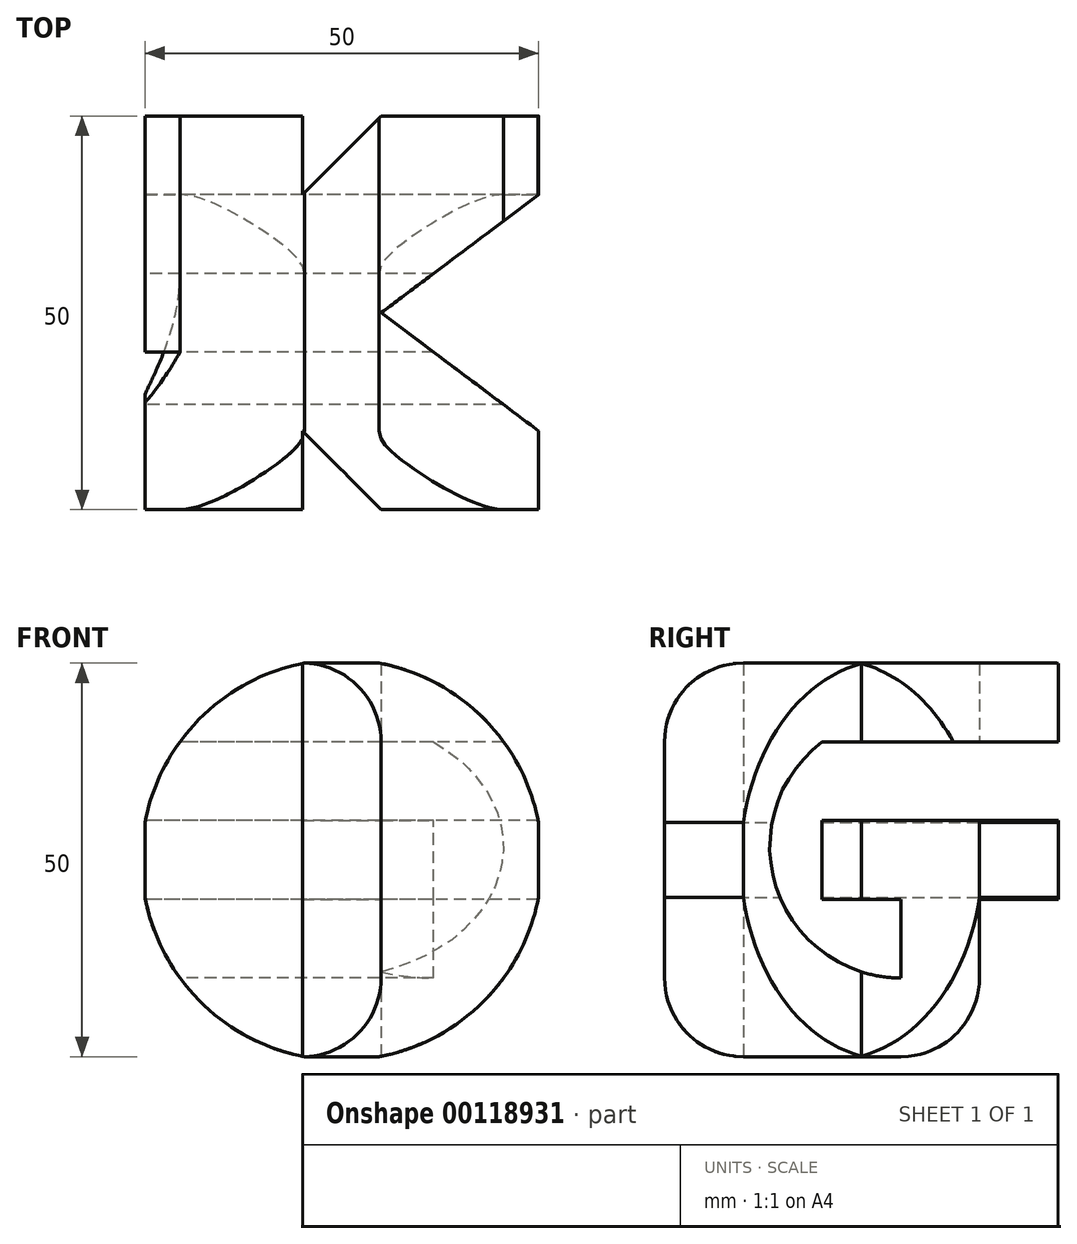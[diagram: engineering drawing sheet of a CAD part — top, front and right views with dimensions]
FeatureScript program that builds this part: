
annotation { "Feature Type Name" : "Feature", "Feature Type Description" : "" }
export const myFeature = defineFeature(function(context is Context, id is Id, definition is map)
    precondition{}
    {
        {
            var Q0;
            Q0=qCreatedBy(makeId("Top.planeOp"),FACE);
            var sketch = newSketch(context, id + "F0", { "sketchPlane" : qUnion([Q0])});
            skLineSegment(sketch, "E0", {"start": v(-25, 25) * mm, "end": v(-25, -25) * mm});
            skLineSegment(sketch, "E1", {"start": v(-25, -25) * mm, "end": v(-5, -25) * mm});
            skLineSegment(sketch, "E2", {"start": v(-5, -15) * mm, "end": v(-5, -25) * mm});
            skLineSegment(sketch, "E3", {"start": v(-5, -15) * mm, "end": v(5, -25) * mm});
            skLineSegment(sketch, "E4", {"start": v(5, -25) * mm, "end": v(25, -25) * mm});
            skLineSegment(sketch, "E5", {"start": v(25, 15) * mm, "end": v(25, 25) * mm});
            skLineSegment(sketch, "E6", {"start": v(-5, 25) * mm, "end": v(-25, 25) * mm});
            skLineSegment(sketch, "E7", {"start": v(-5, 15) * mm, "end": v(5, 25) * mm});
            skLineSegment(sketch, "E8", {"start": v(5, 0) * mm, "end": v(25, -15) * mm});
            skLineSegment(sketch, "E9", {"start": v(25, 15) * mm, "end": v(5, 0) * mm});
            skLineSegment(sketch, "E10", {"start": v(25, -25) * mm, "end": v(25, -15) * mm});
            skLineSegment(sketch, "E11", {"start": v(-5, 15) * mm, "end": v(-5, 25) * mm});
            skLineSegment(sketch, "E12", {"start": v(5, 25) * mm, "end": v(25, 25) * mm});
            skSolve(sketch);
        }
        {
            var Q0;
            Q0=qCreatedBy(makeId("Right.planeOp"),FACE);
            var sketch = newSketch(context, id + "F1", { "sketchPlane" : qUnion([Q0])});
            skLineSegment(sketch, "E13", {"start": v(25, 15) * mm, "end": v(25, 15) * mm});
            skLineSegment(sketch, "E14", {"start": v(25, 15) * mm, "end": v(5, 15) * mm});
            skLineSegment(sketch, "E15", {"start": v(-5, 5) * mm, "end": v(-5, -5) * mm});
            skLineSegment(sketch, "E16", {"start": v(5, -15) * mm, "end": v(5, -15) * mm});
            skLineSegment(sketch, "E17", {"start": v(15, -5) * mm, "end": v(15, -5) * mm});
            skLineSegment(sketch, "E18", {"start": v(-25, 15) * mm, "end": v(-25, -15) * mm});
            skArc(sketch, "E19.filletArc", {"start": v(-15, 25) * mm, "mid": v(-22.07, 22.07) * mm, "end": v(-25, 15) * mm});
            skPoint(sketch, "E20.visualSharp", {"position": v(15, -15) * mm});
            skPoint(sketch, "E21.visualSharp", {"position": v(-5, 15) * mm});
            skArc(sketch, "E22.filletArc", {"start": v(-25, -15) * mm, "mid": v(-22.07, -22.07) * mm, "end": v(-15, -25) * mm});
            skLineSegment(sketch, "E23", {"start": v(25, 15) * mm, "end": v(25, 25) * mm});
            skLineSegment(sketch, "E24", {"start": v(5, -5) * mm, "end": v(5, -15) * mm});
            skLineSegment(sketch, "E25", {"start": v(15, -15) * mm, "end": v(15, -5) * mm});
            skLineSegment(sketch, "E26", {"start": v(15, -5) * mm, "end": v(25, -5) * mm});
            skLineSegment(sketch, "E27", {"start": v(-5, -5) * mm, "end": v(5, -5) * mm});
            skArc(sketch, "E28", {"start": v(5, -25) * mm, "mid": v(12.07, -22.07) * mm, "end": v(15, -15) * mm});
            skLineSegment(sketch, "E29", {"start": v(-15, -25) * mm, "end": v(5, -25) * mm});
            skArc(sketch, "E30", {"start": v(-10, -5) * mm, "mid": v(-4.01, -12.27) * mm, "end": v(5, -15) * mm});
            skArc(sketch, "E31", {"start": v(-5, 15) * mm, "mid": v(-10.81, -3.6) * mm, "end": v(5, -15) * mm});
            skLineSegment(sketch, "E32", {"start": v(-5, 15) * mm, "end": v(25, 15) * mm});
            skLineSegment(sketch, "E33", {"start": v(25, 5) * mm, "end": v(25, -5) * mm});
            skLineSegment(sketch, "E34", {"start": v(-15, 25) * mm, "end": v(25, 25) * mm});
            skLineSegment(sketch, "E35", {"start": v(-5, 5) * mm, "end": v(25, 5) * mm});
            skSolve(sketch);
        }
        {
            var Q0;
            Q0 = qSketchRegion(id + "F0", true);
            extrude(context, id + "F2", {"entities" : qUnion([Q0]), "endBound" : BoundingType.SYMMETRIC, "depth" : 50 * mm});
        }
        {
            var Q0;
            Q0 = qSketchRegion(id + "F1", true);
            extrude(context, id + "F3", {"entities" : qUnion([Q0]), "operationType" : NewBodyOperationType.INTERSECT, "endBound" : BoundingType.SYMMETRIC, "depth" : 50 * mm});
        }
        {
            var Q0;
            Q0=qCreatedBy(makeId("Front.planeOp"),FACE);
            var sketch = newSketch(context, id + "F4", { "sketchPlane" : qUnion([Q0])});
            skCircle(sketch, "E36", {"center": v(0, 0) * mm, "radius": 25.45 * mm});
            skSolve(sketch);
        }
        {
            var Q0;
            Q0 = qSketchRegion(id + "F4", true);
            extrude(context, id + "F5", {"entities" : qUnion([Q0]), "operationType" : NewBodyOperationType.INTERSECT, "endBound" : BoundingType.SYMMETRIC, "depth" : 50 * mm});
        }
    });
